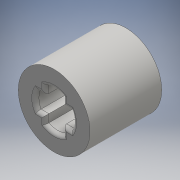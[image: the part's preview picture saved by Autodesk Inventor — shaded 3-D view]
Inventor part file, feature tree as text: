
AUTODESK INVENTOR PART (.ipt)
format: ipt  version: 2016 (Build 200138000, 138)  size: 169,984 bytes
history: native  units: mm
features: extrude x3, sketch x3, fillet x1
ambient origin geometry x8: Origin, YZ Plane, XZ Plane, XY Plane, X Axis, Y Axis, Z Axis, Center Point
bodies: Solid1 (feature_tree)
feature tree (7):
  extrude  "Extrusion1"  Depth=2.0mm
  extrude  "Extrusion2"  Depth=10.0mm
  extrude  "Extrusion3"  Depth=10.0mm TaperAngle=0.0deg
  fillet  "Fillet2"  Radius=5.25mm
  sketch  "Sketch1"  dims[d0=7.0mm d1=2.0mm]
  sketch  "Sketch2"  dims[d2=2.0mm d3=10.0mm]
  sketch  "Sketch3"  dims[d5=5.0mm d6=0.0mm d8=5.0mm d9=0.0mm d10=5.25mm d11=1.3mm d12=1.3mm d13=1.3mm d14=1.3mm d15=5.0mm d16=0.0mm d17=0.5mm d19=10.0mm d20=3.0mm d21=3.0mm d22=1.1mm d23=1.1mm d24=1.1mm d25=1.1mm d26=1.1mm d27=1.1mm d28=1.1mm d29=1.1mm]
